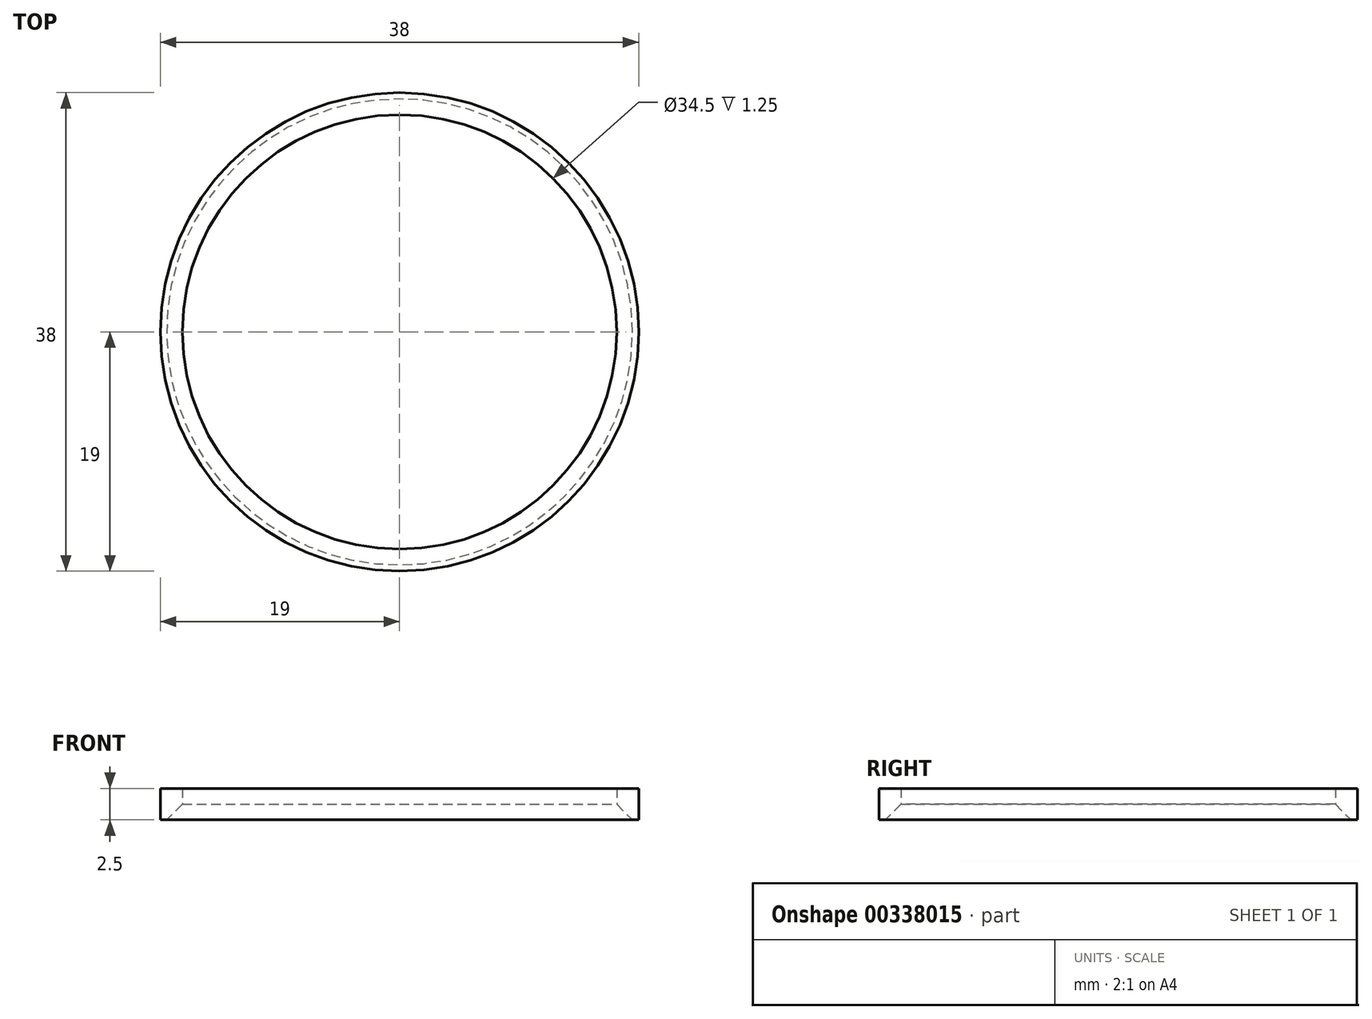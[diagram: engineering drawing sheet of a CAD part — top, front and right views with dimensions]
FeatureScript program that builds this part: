
annotation { "Feature Type Name" : "Feature", "Feature Type Description" : "" }
export const myFeature = defineFeature(function(context is Context, id is Id, definition is map)
    precondition{}
    {
        {
            var Q0;
            Q0=qCreatedBy(makeId("Front.planeOp"),FACE);
            var sketch = newSketch(context, id + "F0", { "sketchPlane" : qUnion([Q0])});
            skLineSegment(sketch, "E0", {"start": v(0, 0) * mm, "end": v(19, 0) * mm, "construction": true});
            skLineSegment(sketch, "E1", {"start": v(19, 0) * mm, "end": v(18.5, 0) * mm});
            skLineSegment(sketch, "E2", {"start": v(19, 0) * mm, "end": v(19, 2.5) * mm});
            skLineSegment(sketch, "E3", {"start": v(19, 2.5) * mm, "end": v(17.25, 2.5) * mm});
            skLineSegment(sketch, "E4", {"start": v(17.25, 2.5) * mm, "end": v(17.25, 1.25) * mm});
            skLineSegment(sketch, "E5", {"start": v(17.25, 1.25) * mm, "end": v(18.5, 0) * mm});
            skLineSegment(sketch, "E6", {"start": v(0, 0) * mm, "end": v(0, 3) * mm, "construction": true});
            skSolve(sketch);
        }
        {
            var Q0;
            Q0 = qSketchRegion(id + "F0", true);
            var Q1;
            Q1=sQuery(id+"F0.wireOp",EDGE,"E6");
            revolve(context, id + "F1", {"entities" : qUnion([Q0]), "axis" : qUnion([Q1]), "revolveType" : RevolveType.FULL});
        }
    });
